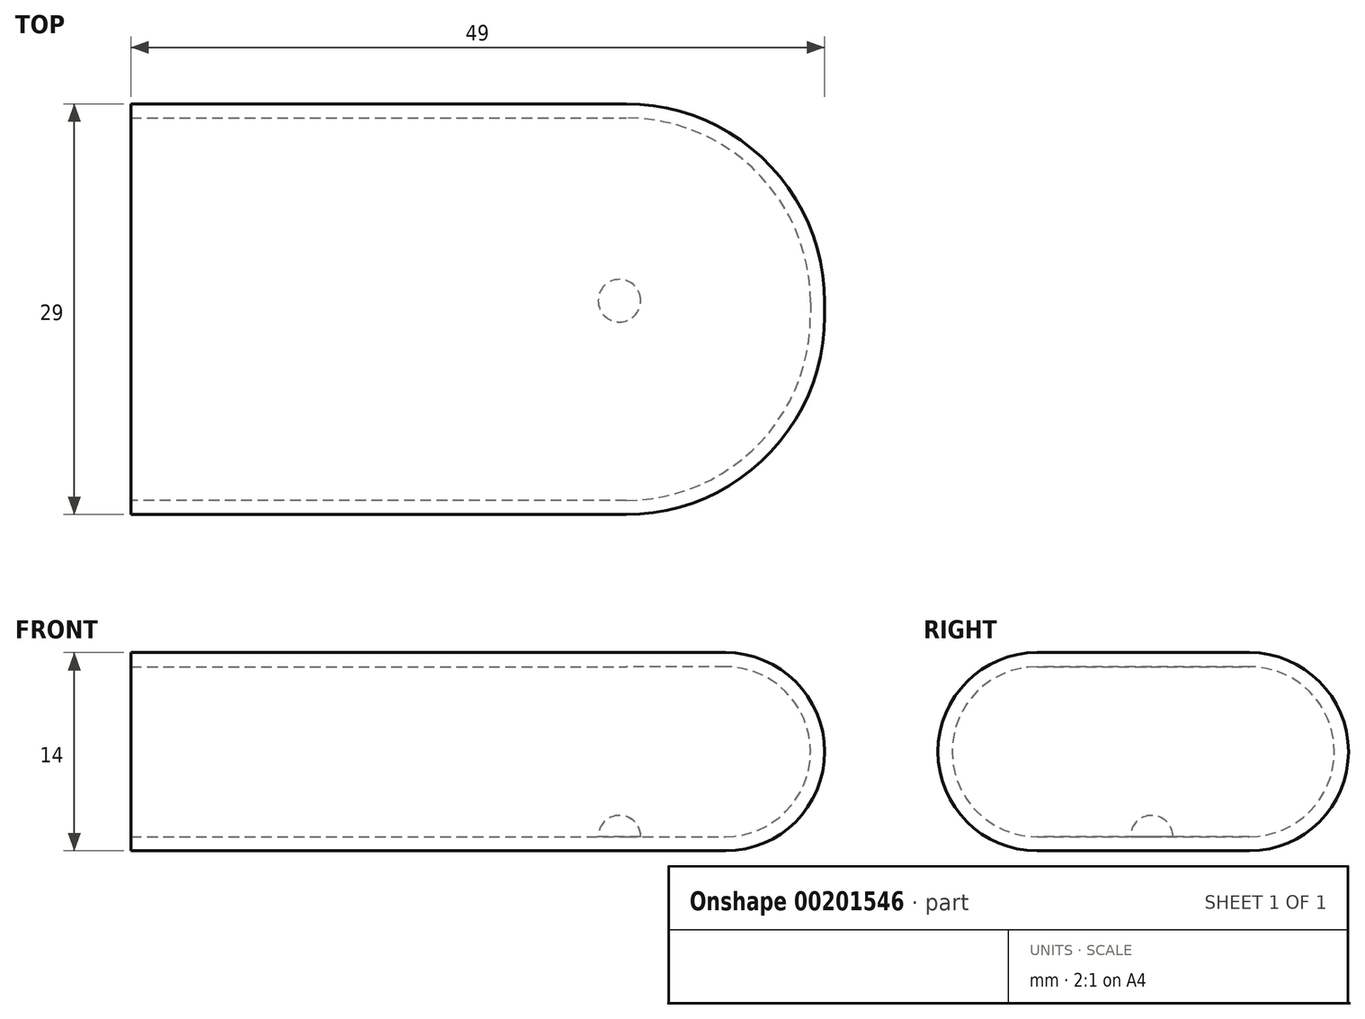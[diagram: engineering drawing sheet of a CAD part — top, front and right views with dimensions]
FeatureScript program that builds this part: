
annotation { "Feature Type Name" : "Feature", "Feature Type Description" : "" }
export const myFeature = defineFeature(function(context is Context, id is Id, definition is map)
    precondition{}
    {
        {
            var Q0;
            Q0=qCreatedBy(makeId("Top.planeOp"),FACE);
            var sketch = newSketch(context, id + "F0", { "sketchPlane" : qUnion([Q0])});
            skLineSegment(sketch, "E0.bottom", {"start": v(-37.91, 17.92) * mm, "end": v(11.09, 17.92) * mm});
            skLineSegment(sketch, "E0.top", {"start": v(-37.91, -11.08) * mm, "end": v(11.09, -11.08) * mm});
            skLineSegment(sketch, "E0.left", {"start": v(-37.91, 17.92) * mm, "end": v(-37.91, -11.08) * mm});
            skLineSegment(sketch, "E0.right", {"start": v(11.09, 17.92) * mm, "end": v(11.09, -11.08) * mm});
            skSolve(sketch);
        }
        {
            var Q0;
            Q0=makeQuery(id+"F0.imprint","IMPRINT",FACE,{"disambiguationData":[TD([[makeQuery(id+"F0.imprint","IMPRINT",EDGE,{"derivedFrom":sQuery(id+"F0.wireOp",EDGE,"E0.bottom")}),-1.0]])]});
            extrude(context, id + "F1", {"entities" : qUnion([Q0]), "depth" : 14 * mm});
        }
        {
            var Q0;
            Q0=makeQuery(id+"F1.opExtrude","SWEPT_EDGE",EDGE,{"disambiguationData":[OSD([sQuery(id+"F0.wireOp",EDGE,"E0.bottom"),sQuery(id+"F0.wireOp",EDGE,"E0.right")])]});
            var Q1;
            Q1=makeQuery(id+"F1.opExtrude","SWEPT_EDGE",EDGE,{"disambiguationData":[OSD([sQuery(id+"F0.wireOp",EDGE,"E0.top"),sQuery(id+"F0.wireOp",EDGE,"E0.right")])]});
            fillet(context, id + "F2", {"entities" : qUnion([Q0, Q1]), "radius" : 14 * mm, "tangentPropagation" : true, "allowEdgeOverflow" : false});
        }
        {
            var Q0;
            Q0=makeQuery(id+"F1.opExtrude","CAP_EDGE",EDGE,{"disambiguationData":[OSD([sQuery(id+"F0.wireOp",EDGE,"E0.bottom")])],"isStart":false});
            var Q1;
            Q1=makeQuery(id+"F1.opExtrude","CAP_EDGE",EDGE,{"disambiguationData":[OSD([sQuery(id+"F0.wireOp",EDGE,"E0.bottom")])],"isStart":true});
            var Q2;
            {var subQ0=sQuery(id+"F0.wireOp",EDGE,"E0.right");var subQ1=sQuery(id+"F0.wireOp",EDGE,"E0.bottom");Q2=makeQuery(id+"F2.opFillet","BLEND_EDGE",EDGE,{"blendedFrom":[makeQuery(id+"F1.opExtrude","SWEPT_EDGE",EDGE,{"disambiguationData":[OSD([subQ1,subQ0])]}),makeQuery(id+"F1.opExtrude","CAP_FACE",FACE,{"disambiguationData":[OSD([subQ1,sQuery(id+"F0.wireOp",EDGE,"E0.top"),sQuery(id+"F0.wireOp",EDGE,"E0.left"),subQ0])],"isStart":false})],"blendedInto":[makeQuery(id+"F1.opExtrude","CAP_FACE",FACE,{"disambiguationData":[OSD([subQ1,sQuery(id+"F0.wireOp",EDGE,"E0.top"),sQuery(id+"F0.wireOp",EDGE,"E0.left"),subQ0])],"isStart":false})]});}
            var Q3;
            {var subQ0=sQuery(id+"F0.wireOp",EDGE,"E0.right");var subQ1=sQuery(id+"F0.wireOp",EDGE,"E0.bottom");Q3=makeQuery(id+"F2.opFillet","BLEND_EDGE",EDGE,{"blendedFrom":[makeQuery(id+"F1.opExtrude","SWEPT_EDGE",EDGE,{"disambiguationData":[OSD([subQ1,subQ0])]}),makeQuery(id+"F1.opExtrude","CAP_FACE",FACE,{"disambiguationData":[OSD([subQ1,sQuery(id+"F0.wireOp",EDGE,"E0.top"),sQuery(id+"F0.wireOp",EDGE,"E0.left"),subQ0])],"isStart":true})],"blendedInto":[makeQuery(id+"F1.opExtrude","CAP_FACE",FACE,{"disambiguationData":[OSD([subQ1,sQuery(id+"F0.wireOp",EDGE,"E0.top"),sQuery(id+"F0.wireOp",EDGE,"E0.left"),subQ0])],"isStart":true})]});}
            var Q4;
            {var subQ0=sQuery(id+"F0.wireOp",EDGE,"E0.right");var subQ1=sQuery(id+"F0.wireOp",EDGE,"E0.top");Q4=makeQuery(id+"F2.opFillet","BLEND_EDGE",EDGE,{"blendedFrom":[makeQuery(id+"F1.opExtrude","SWEPT_EDGE",EDGE,{"disambiguationData":[OSD([subQ1,subQ0])]}),makeQuery(id+"F1.opExtrude","CAP_FACE",FACE,{"disambiguationData":[OSD([sQuery(id+"F0.wireOp",EDGE,"E0.bottom"),subQ1,sQuery(id+"F0.wireOp",EDGE,"E0.left"),subQ0])],"isStart":false})],"blendedInto":[makeQuery(id+"F1.opExtrude","CAP_FACE",FACE,{"disambiguationData":[OSD([sQuery(id+"F0.wireOp",EDGE,"E0.bottom"),subQ1,sQuery(id+"F0.wireOp",EDGE,"E0.left"),subQ0])],"isStart":false})]});}
            var Q5;
            {var subQ0=sQuery(id+"F0.wireOp",EDGE,"E0.right");var subQ1=sQuery(id+"F0.wireOp",EDGE,"E0.top");Q5=makeQuery(id+"F2.opFillet","BLEND_EDGE",EDGE,{"blendedFrom":[makeQuery(id+"F1.opExtrude","SWEPT_EDGE",EDGE,{"disambiguationData":[OSD([subQ1,subQ0])]}),makeQuery(id+"F1.opExtrude","CAP_FACE",FACE,{"disambiguationData":[OSD([sQuery(id+"F0.wireOp",EDGE,"E0.bottom"),subQ1,sQuery(id+"F0.wireOp",EDGE,"E0.left"),subQ0])],"isStart":true})],"blendedInto":[makeQuery(id+"F1.opExtrude","CAP_FACE",FACE,{"disambiguationData":[OSD([sQuery(id+"F0.wireOp",EDGE,"E0.bottom"),subQ1,sQuery(id+"F0.wireOp",EDGE,"E0.left"),subQ0])],"isStart":true})]});}
            var Q6;
            Q6=makeQuery(id+"F1.opExtrude","CAP_EDGE",EDGE,{"disambiguationData":[OSD([sQuery(id+"F0.wireOp",EDGE,"E0.top")])],"isStart":false});
            var Q7;
            Q7=makeQuery(id+"F1.opExtrude","CAP_EDGE",EDGE,{"disambiguationData":[OSD([sQuery(id+"F0.wireOp",EDGE,"E0.top")])],"isStart":true});
            fillet(context, id + "F3", {"entities" : qUnion([Q0, Q1, Q2, Q3, Q4, Q5, Q6, Q7]), "radius" : 7 * mm, "tangentPropagation" : true, "allowEdgeOverflow" : false});
        }
        {
            var Q0;
            Q0=makeQuery(id+"F1.opExtrude","SWEPT_FACE",FACE,{"disambiguationData":[OSD([sQuery(id+"F0.wireOp",EDGE,"E0.left")])]});
            shell(context, id + "F4", {"entities" : qUnion([Q0]), "thickness" : 1 * mm});
        }
        {
            var Q0;
            {var subQ0=sQuery(id+"F0.wireOp",EDGE,"E0.right");var subQ1=sQuery(id+"F0.wireOp",EDGE,"E0.left");var subQ2=sQuery(id+"F0.wireOp",EDGE,"E0.top");var subQ3=sQuery(id+"F0.wireOp",EDGE,"E0.bottom");Q0=makeQuery(id+"F4.opShell","OFFSET_FACE",FACE,{"disambiguationData":[OSD([subQ3,subQ2,subQ1,subQ0]),TDD([makeQuery(id+"F1.opExtrude","CAP_FACE",FACE,{"disambiguationData":[OSD([subQ3,subQ2,subQ1,subQ0])],"isStart":true})])]});}
            var sketch = newSketch(context, id + "F5", { "sketchPlane" : qUnion([Q0])});
            skCircle(sketch, "E1", {"center": v(-3.4, 4.02) * mm, "radius": 1.5 * mm});
            skSolve(sketch);
        }
        {
            var Q0;
            Q0=makeQuery(id+"F5.imprint","IMPRINT",FACE,{"disambiguationData":[TD([[makeQuery(id+"F5.imprint","IMPRINT",EDGE,{"derivedFrom":sQuery(id+"F5.wireOp",EDGE,"E1")}),1.0]])]});
            extrude(context, id + "F6", {"entities" : qUnion([Q0]), "operationType" : NewBodyOperationType.ADD, "depth" : 1.5 * mm});
        }
        {
            var Q0;
            Q0=makeQuery(id+"F6.opExtrude","CAP_EDGE",EDGE,{"disambiguationData":[OSD([sQuery(id+"F5.wireOp",EDGE,"E1")])],"isStart":false});
            fillet(context, id + "F7", {"entities" : qUnion([Q0]), "radius" : 1.5 * mm, "tangentPropagation" : true, "allowEdgeOverflow" : false});
        }
    });
